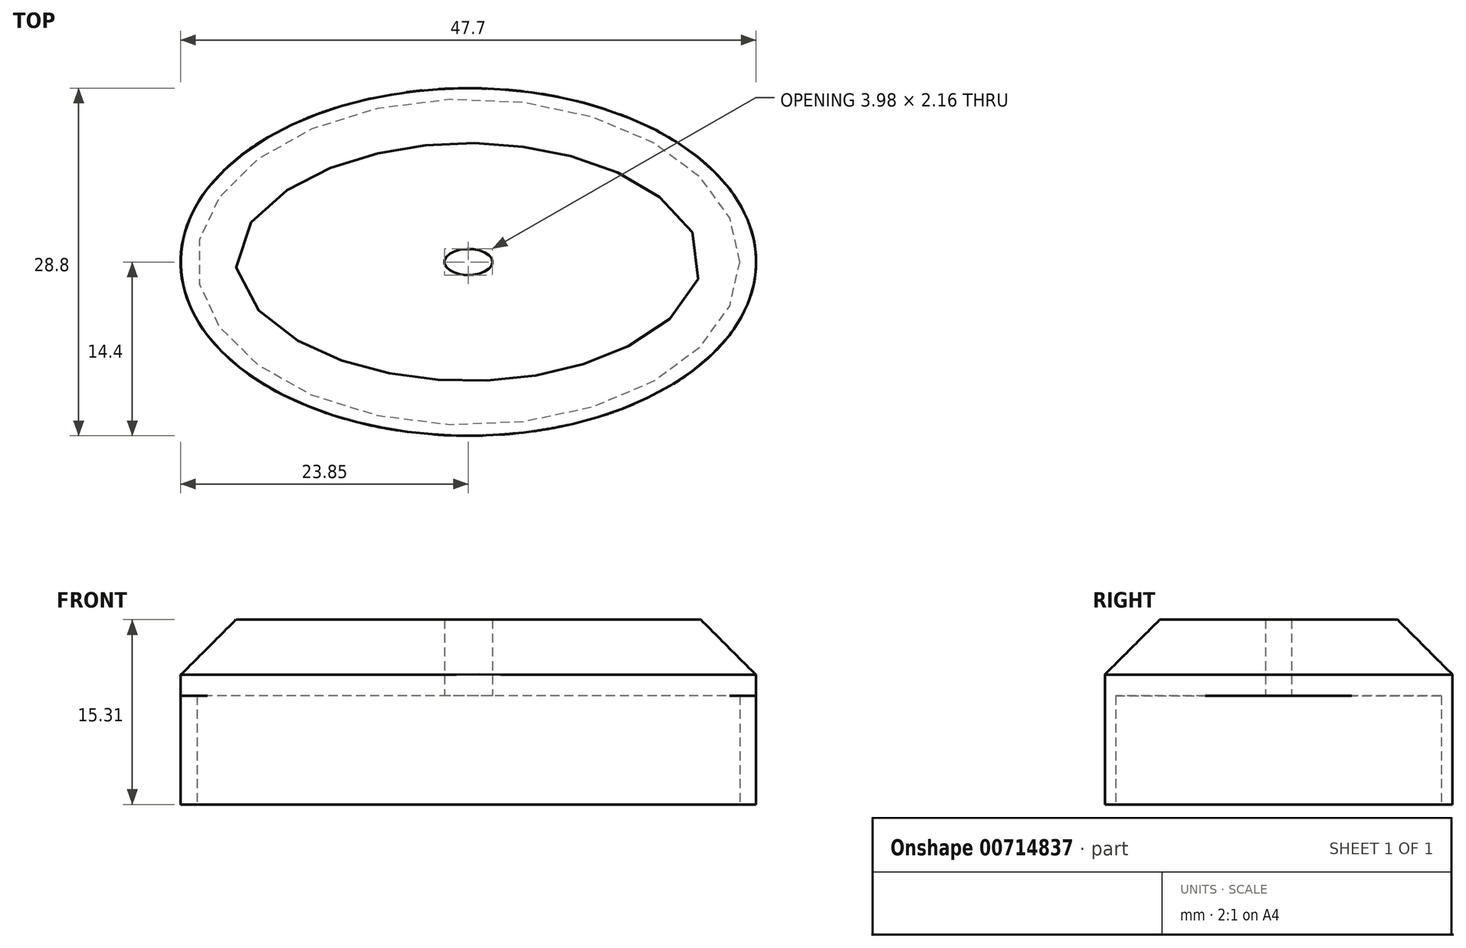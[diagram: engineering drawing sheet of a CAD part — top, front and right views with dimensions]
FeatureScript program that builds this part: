
annotation { "Feature Type Name" : "Feature", "Feature Type Description" : "" }
export const myFeature = defineFeature(function(context is Context, id is Id, definition is map)
    precondition{}
    {
        {
            var Q0;
            Q0=qCreatedBy(makeId("Top.planeOp"),FACE);
            var sketch = newSketch(context, id + "F0", { "sketchPlane" : qUnion([Q0])});
            skEllipse(sketch, "E0", {"center": v(0, 0) * mm, "majorRadius": 25 * mm, "minorRadius": 15 * mm, "majorAxis": v(1, 0)});
            skEllipse(sketch, "E1", {"center": v(0, 0) * mm, "majorRadius": 26.5 * mm, "minorRadius": 16 * mm, "majorAxis": v(1, 0)});
            skSolve(sketch);
        }
        {
            var Q0;
            Q0=makeQuery(id+"F0.imprint","IMPRINT",FACE,{"disambiguationData":[TD([[makeQuery(id+"F0.imprint","IMPRINT",EDGE,{"derivedFrom":sQuery(id+"F0.wireOp",EDGE,"E0")}),-1.0]])]});
            extrude(context, id + "F1", {"entities" : qUnion([Q0]), "depth" : 10 * mm, "offsetDistance" : 25.4 * mm});
        }
        {
            var Q0;
            Q0=makeQuery(id+"F1.opExtrude","CAP_FACE",FACE,{"disambiguationData":[OSD([sQuery(id+"F0.wireOp",EDGE,"E0"),sQuery(id+"F0.wireOp",EDGE,"E1")])],"isStart":false});
            var sketch = newSketch(context, id + "F2", { "sketchPlane" : qUnion([Q0])});
            skEllipse(sketch, "E2", {"center": v(0, 0) * mm, "majorRadius": 26.49 * mm, "minorRadius": 16.03 * mm, "majorAxis": v(1, 0)});
            skEllipse(sketch, "E3", {"center": v(0, 0) * mm, "majorRadius": 2.2 * mm, "minorRadius": 1.2 * mm, "majorAxis": v(1, 0)});
            skSolve(sketch);
        }
        {
            var Q0;
            Q0=makeQuery(id+"F2.imprint","IMPRINT",FACE,{"disambiguationData":[TD([[makeQuery(id+"F2.imprint","IMPRINT",EDGE,{"derivedFrom":sQuery(id+"F2.wireOp",EDGE,"E3")}),-1.0]])]});
            cPlane(context, id + "F3", {"entities" : qUnion([Q0]), "cplaneType" : CPlaneType.OFFSET, "offset" : 12.7 * mm, "width" : 152.4 * mm, "height" : 152.4 * mm});
        }
        {
            var Q0;
            Q0=makeQuery(id+"F2.imprint","IMPRINT",FACE,{"disambiguationData":[TD([[makeQuery(id+"F2.imprint","IMPRINT",EDGE,{"derivedFrom":makeQuery(id+"F1.opExtrude","CAP_EDGE",EDGE,{"disambiguationData":[OSD([sQuery(id+"F0.wireOp",EDGE,"E0")])],"isStart":false})}),-1.0]])]});
            var Q1;
            Q1=makeQuery(id+"F2.imprint","IMPRINT",FACE,{"disambiguationData":[TD([[makeQuery(id+"F2.imprint","IMPRINT",EDGE,{"derivedFrom":sQuery(id+"F2.wireOp",EDGE,"E3")}),-1.0]])]});
            extrude(context, id + "F4", {"entities" : qUnion([Q0, Q1]), "operationType" : NewBodyOperationType.ADD, "depth" : 7 * mm, "offsetDistance" : 25.4 * mm});
        }
        {
            var Q0;
            {var subQ0=sQuery(id+"F2.wireOp",EDGE,"E2");var subQ1=makeQuery(id+"F1.opExtrude","CAP_EDGE",EDGE,{"disambiguationData":[OSD([sQuery(id+"F0.wireOp",EDGE,"E1")])],"isStart":false});Q0=makeQuery(id+"F4.opExtrude","CAP_EDGE",EDGE,{"disambiguationData":[OSD([subQ0]),TDD([makeQuery(id+"F2.imprint","IMPRINT",EDGE,{"disambiguationData":[TD([[makeQuery(id+"F2.imprint","INTERSECT",VERTEX,{"disambiguationData":[OD(0.0)],"derivedFrom":[subQ1,subQ0]}),-1.0]])],"derivedFrom":subQ0})])],"isStart":false});}
            chamfer(context, id + "F5", {"entities" : qUnion([Q0]), "width" : 5.08 * mm, "tangentPropagation" : true});
        }
        {
            var Q0;
            Q0=makeQuery(id+"F1.opExtrude","SWEPT_BODY",BODY,{"disambiguationData":[OSD([sQuery(id+"F0.wireOp",EDGE,"E0"),sQuery(id+"F0.wireOp",EDGE,"E1")])]});
            var Q1;
            Q1=sQuery(id+"F0.wireOp",VERTEX,"E1.center");
            transform(context, id + "F6", {"entities" : qUnion([Q0]), "transformType" : TransformType.SCALE_UNIFORMLY, "scale" : .9, "scalePoint" : qUnion([Q1]), "makeCopy" : false});
        }
    });
